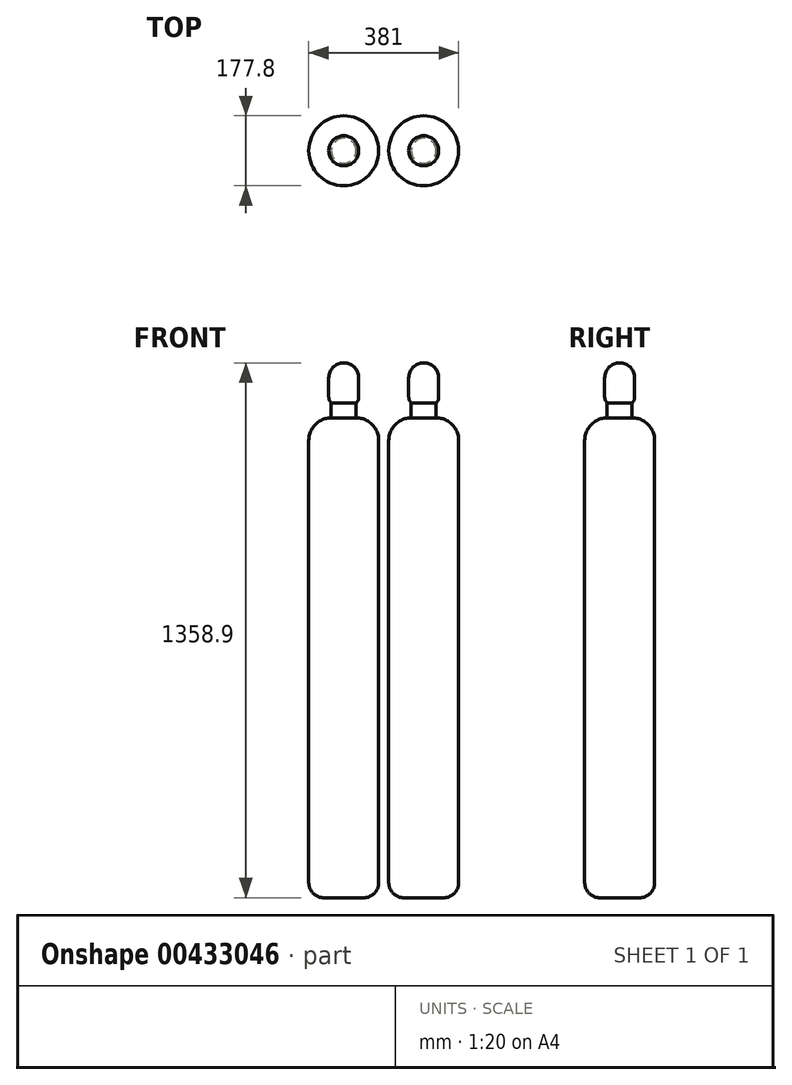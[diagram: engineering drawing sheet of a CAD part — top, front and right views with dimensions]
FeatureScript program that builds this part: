
annotation { "Feature Type Name" : "Feature", "Feature Type Description" : "" }
export const myFeature = defineFeature(function(context is Context, id is Id, definition is map)
    precondition{}
    {
        {
            var Q0;
            Q0=qCreatedBy(makeId("Front.planeOp"),FACE);
            var sketch = newSketch(context, id + "F0", { "sketchPlane" : qUnion([Q0])});
            skLineSegment(sketch, "E0", {"start": v(0, -1219.2) * mm, "end": v(0, 139.7) * mm});
            skLineSegment(sketch, "E1", {"start": v(-88.9, -57.15) * mm, "end": v(-88.9, -1181.1) * mm});
            skLineSegment(sketch, "E2", {"start": v(-38.1, 101.6) * mm, "end": v(-38.1, 52.86) * mm});
            skArc(sketch, "E3", {"start": v(0, 139.7) * mm, "mid": v(-26.94, 128.54) * mm, "end": v(-38.1, 101.6) * mm});
            skArc(sketch, "E4", {"start": v(-38.1, 52.86) * mm, "mid": v(-36.45, 44.82) * mm, "end": v(-31.75, 38.1) * mm});
            skLineSegment(sketch, "E5", {"start": v(-31.75, 38.1) * mm, "end": v(-31.75, 0) * mm});
            skArc(sketch, "E6", {"start": v(-31.75, 0) * mm, "mid": v(-72.16, -16.74) * mm, "end": v(-88.9, -57.15) * mm});
            skLineSegment(sketch, "E7", {"start": v(0, -1219.2) * mm, "end": v(-50.8, -1219.2) * mm});
            skArc(sketch, "E8", {"start": v(-88.9, -1181.1) * mm, "mid": v(-77.74, -1208.04) * mm, "end": v(-50.8, -1219.2) * mm});
            skLineSegment(sketch, "E9", {"start": v(0, 362.2) * mm, "end": v(0, -1554.57) * mm, "construction": true});
            skSolve(sketch);
        }
        {
            var Q0;
            Q0 = qSketchRegion(id + "F0", true);
            var Q1;
            Q1=sQuery(id+"F0.wireOp",EDGE,"E9");
            revolve(context, id + "F1", {"entities" : qUnion([Q0]), "axis" : qUnion([Q1]), "revolveType" : RevolveType.FULL});
        }
        {
            var Q0;
            Q0=qCreatedBy(makeId("Front.planeOp"),FACE);
            var sketch = newSketch(context, id + "F2", { "sketchPlane" : qUnion([Q0])});
            skLineSegment(sketch, "E10", {"start": v(203.2, -1219.2) * mm, "end": v(203.2, 139.7) * mm});
            skLineSegment(sketch, "E11", {"start": v(114.3, -57.15) * mm, "end": v(114.3, -1181.1) * mm});
            skLineSegment(sketch, "E12", {"start": v(165.1, 101.6) * mm, "end": v(165.1, 52.86) * mm});
            skArc(sketch, "E13", {"start": v(203.2, 139.7) * mm, "mid": v(176.26, 128.54) * mm, "end": v(165.1, 101.6) * mm});
            skArc(sketch, "E14", {"start": v(165.1, 52.86) * mm, "mid": v(166.75, 44.82) * mm, "end": v(171.45, 38.1) * mm});
            skLineSegment(sketch, "E15", {"start": v(171.45, 38.1) * mm, "end": v(171.45, 0) * mm});
            skArc(sketch, "E16", {"start": v(171.45, 0) * mm, "mid": v(131.04, -16.74) * mm, "end": v(114.3, -57.15) * mm});
            skLineSegment(sketch, "E17", {"start": v(203.2, -1219.2) * mm, "end": v(152.4, -1219.2) * mm});
            skArc(sketch, "E18", {"start": v(114.3, -1181.1) * mm, "mid": v(125.46, -1208.04) * mm, "end": v(152.4, -1219.2) * mm});
            skLineSegment(sketch, "E19", {"start": v(203.2, 362.2) * mm, "end": v(203.2, -1554.57) * mm, "construction": true});
            skSolve(sketch);
        }
        {
            var Q0;
            Q0=makeQuery(id+"F2.imprint","IMPRINT",FACE,{"disambiguationData":[TD([[makeQuery(id+"F2.imprint","IMPRINT",EDGE,{"derivedFrom":sQuery(id+"F2.wireOp",EDGE,"E10")}),1.0]])]});
            var Q1;
            Q1=sQuery(id+"F2.wireOp",EDGE,"E19");
            revolve(context, id + "F3", {"entities" : qUnion([Q0]), "axis" : qUnion([Q1]), "revolveType" : RevolveType.FULL});
        }
    });
